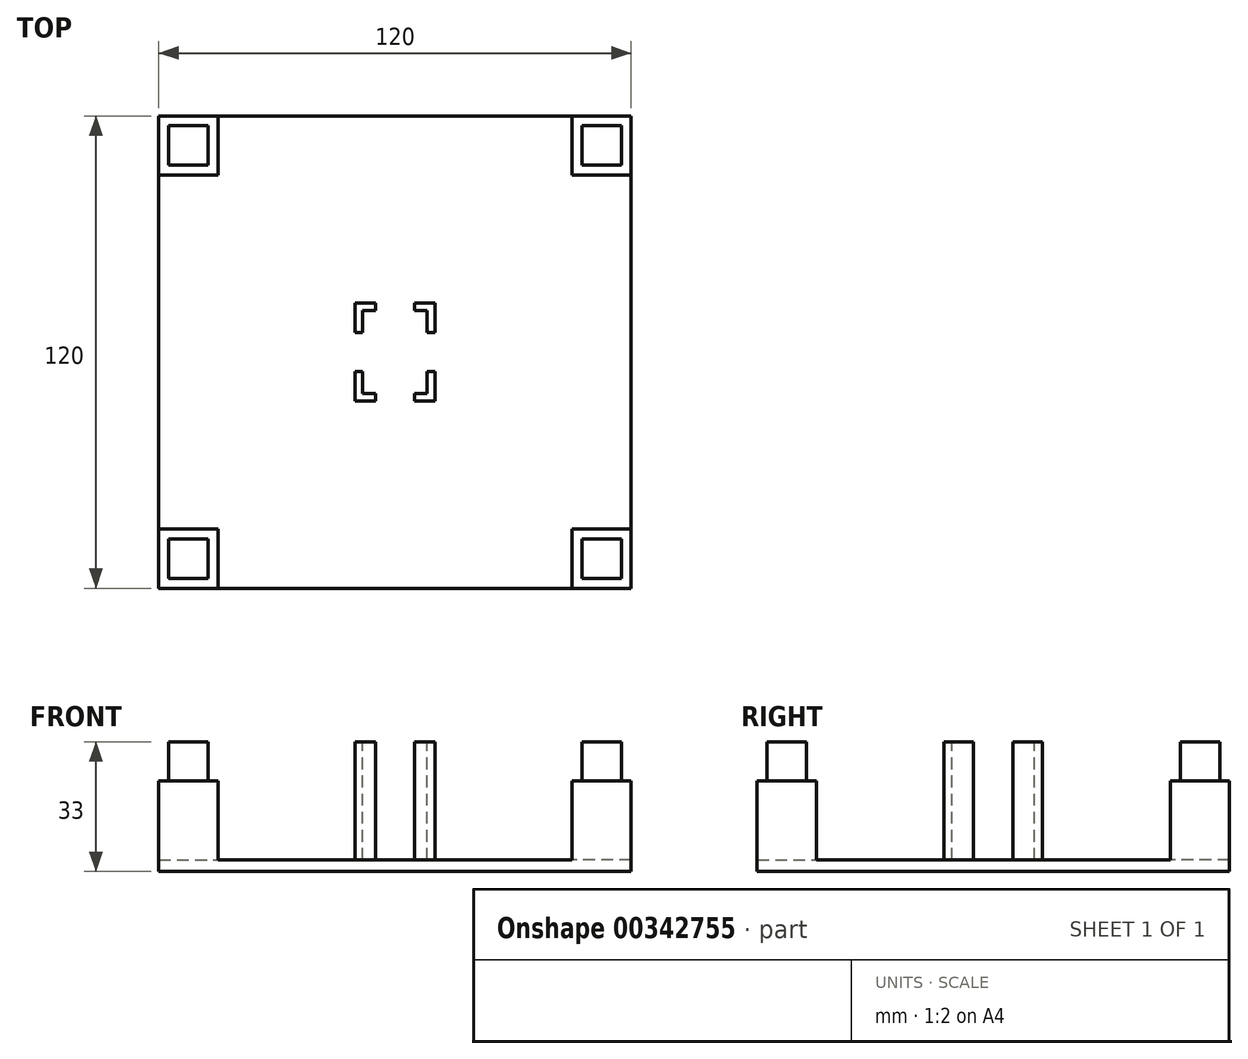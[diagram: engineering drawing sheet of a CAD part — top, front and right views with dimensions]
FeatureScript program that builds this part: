
annotation { "Feature Type Name" : "Feature", "Feature Type Description" : "" }
export const myFeature = defineFeature(function(context is Context, id is Id, definition is map)
    precondition{}
    {
        {
            var Q0;
            Q0=qCreatedBy(makeId("Top.planeOp"),FACE);
            var sketch = newSketch(context, id + "F0", { "sketchPlane" : qUnion([Q0])});
            skLineSegment(sketch, "E0.bottom", {"start": v(60, 60) * mm, "end": v(-60, 60) * mm});
            skLineSegment(sketch, "E0.top", {"start": v(60, -60) * mm, "end": v(-60, -60) * mm});
            skLineSegment(sketch, "E0.left", {"start": v(60, 60) * mm, "end": v(60, -60) * mm});
            skLineSegment(sketch, "E0.right", {"start": v(-60, 60) * mm, "end": v(-60, -60) * mm});
            skPoint(sketch, "E0.middle", {"position": v(0, 0) * mm});
            skSolve(sketch);
        }
        {
            var Q0;
            Q0 = qSketchRegion(id + "F0", true);
            extrude(context, id + "F1", {"entities" : qUnion([Q0]), "depth" : 3 * mm});
        }
        {
            var Q0;
            Q0=makeQuery(id+"F1.opExtrude","CAP_FACE",FACE,{"disambiguationData":[OSD([sQuery(id+"F0.wireOp",EDGE,"E0.bottom"),sQuery(id+"F0.wireOp",EDGE,"E0.top"),sQuery(id+"F0.wireOp",EDGE,"E0.left"),sQuery(id+"F0.wireOp",EDGE,"E0.right")])],"isStart":false});
            var sketch = newSketch(context, id + "F2", { "sketchPlane" : qUnion([Q0])});
            skLineSegment(sketch, "E1.bottom", {"start": v(-60, 60) * mm, "end": v(-45, 60) * mm});
            skLineSegment(sketch, "E1.top", {"start": v(-60, 45) * mm, "end": v(-45, 45) * mm});
            skLineSegment(sketch, "E1.left", {"start": v(-60, 60) * mm, "end": v(-60, 45) * mm});
            skLineSegment(sketch, "E1.right", {"start": v(-45, 60) * mm, "end": v(-45, 45) * mm});
            skLineSegment(sketch, "E2.bottom", {"start": v(-60, -60) * mm, "end": v(-45, -60) * mm});
            skLineSegment(sketch, "E2.top", {"start": v(-60, -45) * mm, "end": v(-45, -45) * mm});
            skLineSegment(sketch, "E2.left", {"start": v(-60, -60) * mm, "end": v(-60, -45) * mm});
            skLineSegment(sketch, "E2.right", {"start": v(-45, -60) * mm, "end": v(-45, -45) * mm});
            skLineSegment(sketch, "E3.bottom", {"start": v(60, -60) * mm, "end": v(45, -60) * mm});
            skLineSegment(sketch, "E3.top", {"start": v(60, -45) * mm, "end": v(45, -45) * mm});
            skLineSegment(sketch, "E3.left", {"start": v(60, -60) * mm, "end": v(60, -45) * mm});
            skLineSegment(sketch, "E3.right", {"start": v(45, -60) * mm, "end": v(45, -45) * mm});
            skLineSegment(sketch, "E4.bottom", {"start": v(60, 60) * mm, "end": v(45, 60) * mm});
            skLineSegment(sketch, "E4.top", {"start": v(60, 45) * mm, "end": v(45, 45) * mm});
            skLineSegment(sketch, "E4.left", {"start": v(60, 60) * mm, "end": v(60, 45) * mm});
            skLineSegment(sketch, "E4.right", {"start": v(45, 60) * mm, "end": v(45, 45) * mm});
            skSolve(sketch);
        }
        {
            var Q0;
            Q0 = qSketchRegion(id + "F2", true);
            extrude(context, id + "F3", {"entities" : qUnion([Q0]), "operationType" : NewBodyOperationType.ADD, "depth" : 20 * mm});
        }
        {
            var Q0;
            Q0=makeQuery(id+"F3.opExtrude","CAP_FACE",FACE,{"disambiguationData":[OSD([sQuery(id+"F2.wireOp",EDGE,"E2.bottom"),sQuery(id+"F2.wireOp",EDGE,"E2.top"),sQuery(id+"F2.wireOp",EDGE,"E2.left"),sQuery(id+"F2.wireOp",EDGE,"E2.right")])],"isStart":false});
            var sketch = newSketch(context, id + "F4", { "sketchPlane" : qUnion([Q0])});
            skLineSegment(sketch, "E5.bottom", {"start": v(-47.5, -47.5) * mm, "end": v(-57.5, -47.5) * mm});
            skLineSegment(sketch, "E5.top", {"start": v(-47.5, -57.5) * mm, "end": v(-57.5, -57.5) * mm});
            skLineSegment(sketch, "E5.left", {"start": v(-47.5, -47.5) * mm, "end": v(-47.5, -57.5) * mm});
            skLineSegment(sketch, "E5.right", {"start": v(-57.5, -47.5) * mm, "end": v(-57.5, -57.5) * mm});
            skPoint(sketch, "E5.middle", {"position": v(-52.5, -52.5) * mm});
            skPoint(sketch, "E5.middle.positionSnap0", {"position": v(-60, -52.5) * mm});
            skPoint(sketch, "E5.middle.positionSnap1", {"position": v(-52.5, -45) * mm});
            skPoint(sketch, "E5.centerSnap0", {"position": v(-60, -52.5) * mm});
            skPoint(sketch, "E5.centerSnap1", {"position": v(-52.5, -45) * mm});
            skLineSegment(sketch, "E6.bottom", {"start": v(47.5, -47.5) * mm, "end": v(57.5, -47.5) * mm});
            skLineSegment(sketch, "E6.top", {"start": v(47.5, -57.5) * mm, "end": v(57.5, -57.5) * mm});
            skLineSegment(sketch, "E6.left", {"start": v(47.5, -47.5) * mm, "end": v(47.5, -57.5) * mm});
            skLineSegment(sketch, "E6.right", {"start": v(57.5, -47.5) * mm, "end": v(57.5, -57.5) * mm});
            skPoint(sketch, "E6.middle", {"position": v(52.5, -52.5) * mm});
            skPoint(sketch, "E6.middle.positionSnap0", {"position": v(-45, -52.5) * mm});
            skPoint(sketch, "E6.centerSnap0", {"position": v(-45, -52.5) * mm});
            skLineSegment(sketch, "E7.bottom", {"start": v(-47.5, 47.5) * mm, "end": v(-57.5, 47.5) * mm});
            skLineSegment(sketch, "E7.top", {"start": v(-47.5, 57.5) * mm, "end": v(-57.5, 57.5) * mm});
            skLineSegment(sketch, "E7.left", {"start": v(-47.5, 47.5) * mm, "end": v(-47.5, 57.5) * mm});
            skLineSegment(sketch, "E7.right", {"start": v(-57.5, 47.5) * mm, "end": v(-57.5, 57.5) * mm});
            skPoint(sketch, "E7.middle", {"position": v(-52.5, 52.5) * mm});
            skLineSegment(sketch, "E8.bottom", {"start": v(57.5, 47.5) * mm, "end": v(47.5, 47.5) * mm});
            skLineSegment(sketch, "E8.top", {"start": v(57.5, 57.5) * mm, "end": v(47.5, 57.5) * mm});
            skLineSegment(sketch, "E8.left", {"start": v(57.5, 47.5) * mm, "end": v(57.5, 57.5) * mm});
            skLineSegment(sketch, "E8.right", {"start": v(47.5, 47.5) * mm, "end": v(47.5, 57.5) * mm});
            skPoint(sketch, "E8.middle", {"position": v(52.5, 52.5) * mm});
            skSolve(sketch);
        }
        {
            var Q0;
            Q0 = qSketchRegion(id + "F4", true);
            extrude(context, id + "F5", {"entities" : qUnion([Q0]), "operationType" : NewBodyOperationType.ADD, "depth" : 10 * mm});
        }
        {
            var Q0;
            Q0=qCreatedBy(makeId("Top.planeOp"),FACE);
            var sketch = newSketch(context, id + "F6", { "sketchPlane" : qUnion([Q0])});
            skLineSegment(sketch, "E9.bottom", {"start": v(-10.2, -12.5) * mm, "end": v(10.2, -12.5) * mm});
            skLineSegment(sketch, "E9.top", {"start": v(-10.2, 12.5) * mm, "end": v(10.2, 12.5) * mm});
            skLineSegment(sketch, "E9.left", {"start": v(-10.2, -12.5) * mm, "end": v(-10.2, 12.5) * mm});
            skLineSegment(sketch, "E9.right", {"start": v(10.2, -12.5) * mm, "end": v(10.2, 12.5) * mm});
            skPoint(sketch, "E9.middle", {"position": v(0, 0) * mm});
            skSolve(sketch);
        }
        {
            var Q0;
            Q0 = qSketchRegion(id + "F6", true);
            extrude(context, id + "F7", {"entities" : qUnion([Q0]), "operationType" : NewBodyOperationType.ADD, "depth" : 33 * mm});
        }
        {
            var Q0;
            Q0=makeQuery(id+"F7.opExtrude","CAP_FACE",FACE,{"disambiguationData":[OSD([sQuery(id+"F6.wireOp",EDGE,"E9.bottom"),sQuery(id+"F6.wireOp",EDGE,"E9.top"),sQuery(id+"F6.wireOp",EDGE,"E9.left"),sQuery(id+"F6.wireOp",EDGE,"E9.right")])],"isStart":false});
            var sketch = newSketch(context, id + "F8", { "sketchPlane" : qUnion([Q0])});
            skLineSegment(sketch, "E10.bottom", {"start": v(8.2, -10.5) * mm, "end": v(-8.2, -10.5) * mm});
            skLineSegment(sketch, "E10.top", {"start": v(8.2, 10.5) * mm, "end": v(-8.2, 10.5) * mm});
            skLineSegment(sketch, "E10.left", {"start": v(8.2, -10.5) * mm, "end": v(8.2, 10.5) * mm});
            skLineSegment(sketch, "E10.right", {"start": v(-8.2, -10.5) * mm, "end": v(-8.2, 10.5) * mm});
            skPoint(sketch, "E10.middle", {"position": v(0, 0) * mm});
            skSolve(sketch);
        }
        {
            var Q0;
            Q0 = qSketchRegion(id + "F8", true);
            extrude(context, id + "F9", {"entities" : qUnion([Q0]), "operationType" : NewBodyOperationType.REMOVE, "oppositeDirection" : true, "depth" : 30 * mm});
        }
        {
            var Q0;
            Q0=makeQuery(id+"F7.opExtrude","CAP_FACE",FACE,{"disambiguationData":[OSD([sQuery(id+"F6.wireOp",EDGE,"E9.bottom"),sQuery(id+"F6.wireOp",EDGE,"E9.top"),sQuery(id+"F6.wireOp",EDGE,"E9.left"),sQuery(id+"F6.wireOp",EDGE,"E9.right")])],"isStart":false});
            var sketch = newSketch(context, id + "F10", { "sketchPlane" : qUnion([Q0])});
            skLineSegment(sketch, "E11.bottom", {"start": v(10.2, -5) * mm, "end": v(-10.2, -5) * mm});
            skLineSegment(sketch, "E11.top", {"start": v(10.2, 5) * mm, "end": v(-10.2, 5) * mm});
            skLineSegment(sketch, "E11.left", {"start": v(10.2, -5) * mm, "end": v(10.2, 5) * mm});
            skLineSegment(sketch, "E11.right", {"start": v(-10.2, -5) * mm, "end": v(-10.2, 5) * mm});
            skPoint(sketch, "E11.middle", {"position": v(0, 0) * mm});
            skSolve(sketch);
        }
        {
            var Q0;
            Q0 = qSketchRegion(id + "F10", true);
            extrude(context, id + "F11", {"entities" : qUnion([Q0]), "operationType" : NewBodyOperationType.REMOVE, "oppositeDirection" : true, "depth" : 30 * mm});
        }
        {
            var Q0;
            {var subQ0=sQuery(id+"F6.wireOp",EDGE,"E9.right");var subQ1=sQuery(id+"F6.wireOp",EDGE,"E9.left");var subQ2=sQuery(id+"F6.wireOp",EDGE,"E9.top");Q0=makeQuery(id+"F11.boolean.opBoolean","SPLIT",FACE,{"disambiguationData":[TD([makeQuery(id+"F7.opExtrude","SWEPT_FACE",FACE,{"disambiguationData":[OSD([subQ2])]})])],"derivedFrom":makeQuery(id+"F7.opExtrude","CAP_FACE",FACE,{"disambiguationData":[OSD([sQuery(id+"F6.wireOp",EDGE,"E9.bottom"),subQ2,subQ1,subQ0])],"isStart":false})});}
            var sketch = newSketch(context, id + "F12", { "sketchPlane" : qUnion([Q0])});
            skLineSegment(sketch, "E12.bottom", {"start": v(5, 12.5) * mm, "end": v(-5, 12.5) * mm});
            skLineSegment(sketch, "E12.top", {"start": v(5, -12.5) * mm, "end": v(-5, -12.5) * mm});
            skLineSegment(sketch, "E12.left", {"start": v(5, 12.5) * mm, "end": v(5, -12.5) * mm});
            skLineSegment(sketch, "E12.right", {"start": v(-5, 12.5) * mm, "end": v(-5, -12.5) * mm});
            skPoint(sketch, "E12.middle", {"position": v(0, 0) * mm});
            skSolve(sketch);
        }
        {
            var Q0;
            Q0 = qSketchRegion(id + "F12", true);
            extrude(context, id + "F13", {"entities" : qUnion([Q0]), "operationType" : NewBodyOperationType.REMOVE, "oppositeDirection" : true, "depth" : 30 * mm});
        }
    });
